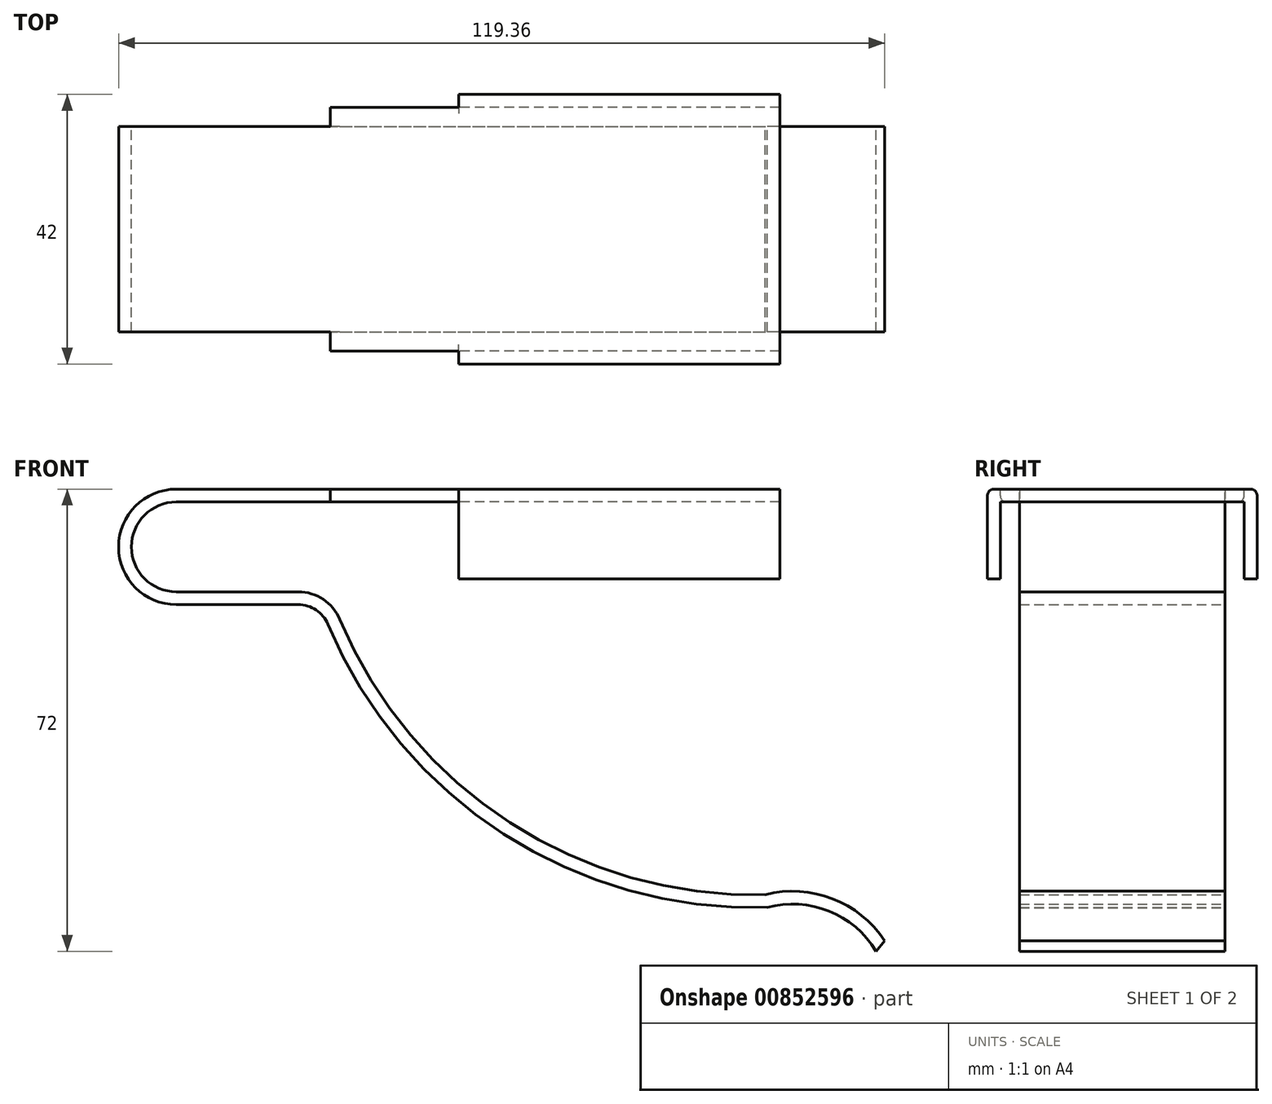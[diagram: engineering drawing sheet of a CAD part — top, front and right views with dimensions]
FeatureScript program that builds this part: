
annotation { "Feature Type Name" : "Feature", "Feature Type Description" : "" }
export const myFeature = defineFeature(function(context is Context, id is Id, definition is map)
    precondition{}
    {
        {
            var Q0;
            Q0=qCreatedBy(makeId("Front.planeOp"),FACE);
            var sketch = newSketch(context, id + "F0", { "sketchPlane" : qUnion([Q0])});
            skArc(sketch, "E0", {"start": v(0, 18) * mm, "mid": v(-9, 9) * mm, "end": v(0, 0) * mm});
            skLineSegment(sketch, "E1", {"start": v(0, 18) * mm, "end": v(94, 18) * mm});
            skLineSegment(sketch, "E2", {"start": v(0, 0) * mm, "end": v(19, 0) * mm});
            skArc(sketch, "E3", {"start": v(23.61, -3.06) * mm, "mid": v(50.99, -35.72) * mm, "end": v(92.03, -47.17) * mm});
            skArc(sketch, "E4", {"start": v(109.01, -54) * mm, "mid": v(101.66, -47.74) * mm, "end": v(92.03, -47.17) * mm});
            skPoint(sketch, "E5.visualSharp", {"position": v(22.4, 0) * mm});
            skArc(sketch, "E5.filletArc", {"start": v(23.61, -3.06) * mm, "mid": v(21.77, -0.84) * mm, "end": v(19, 0) * mm});
            skLineSegment(sketch, "E6.0", {"start": v(0, 16) * mm, "end": v(94, 16) * mm});
            skArc(sketch, "E6.1", {"start": v(0, 16) * mm, "mid": v(-7, 9) * mm, "end": v(0, 2) * mm});
            skArc(sketch, "E6.3", {"start": v(25.45, -2.3) * mm, "mid": v(51.98, -33.97) * mm, "end": v(91.74, -45.18) * mm});
            skArc(sketch, "E6.4", {"start": v(25.45, -2.3) * mm, "mid": v(22.88, 0.83) * mm, "end": v(19, 2) * mm});
            skLineSegment(sketch, "E6.5", {"start": v(0, 2) * mm, "end": v(19, 2) * mm});
            skLineSegment(sketch, "E7", {"start": v(94, 18) * mm, "end": v(94, 16) * mm});
            skLineSegment(sketch, "E8", {"start": v(110.36, -52.4) * mm, "end": v(109.01, -54) * mm});
            skPoint(sketch, "E9", {"position": v(0, 0) * mm});
            skArc(sketch, "E10.0", {"start": v(110.36, -52.4) * mm, "mid": v(102.2, -45.8) * mm, "end": v(91.74, -45.18) * mm});
            skSolve(sketch);
        }
        {
            var Q0;
            Q0=makeQuery(id+"F0.imprint","IMPRINT",FACE,{"disambiguationData":[TD([[makeQuery(id+"F0.imprint","IMPRINT",EDGE,{"derivedFrom":sQuery(id+"F0.wireOp",EDGE,"E0")}),1.0]])]});
            extrude(context, id + "F1", {"entities" : qUnion([Q0]), "depth" : 16 * mm, "offsetDistance" : 25 * mm});
        }
        {
            var Q0;
            Q0=makeQuery(id+"F1.opExtrude","SWEPT_FACE",FACE,{"disambiguationData":[OSD([sQuery(id+"F0.wireOp",EDGE,"E1")])]});
            var sketch = newSketch(context, id + "F2", { "sketchPlane" : qUnion([Q0])});
            skLineSegment(sketch, "E11.bottom", {"start": v(94, -16) * mm, "end": v(24, -16) * mm});
            skLineSegment(sketch, "E11.top", {"start": v(94, -19) * mm, "end": v(24, -19) * mm});
            skLineSegment(sketch, "E11.left", {"start": v(94, -16) * mm, "end": v(94, -19) * mm});
            skLineSegment(sketch, "E11.right", {"start": v(24, -16) * mm, "end": v(24, -19) * mm});
            skSolve(sketch);
        }
        {
            var Q0;
            Q0=makeQuery(id+"F2.imprint","IMPRINT",FACE,{"disambiguationData":[TD([[makeQuery(id+"F2.imprint","IMPRINT",EDGE,{"derivedFrom":sQuery(id+"F2.wireOp",EDGE,"E11.bottom")}),-1.0]])]});
            extrude(context, id + "F3", {"entities" : qUnion([Q0]), "operationType" : NewBodyOperationType.ADD, "oppositeDirection" : true, "depth" : 2 * mm, "offsetDistance" : 25 * mm});
        }
        {
            var Q0;
            Q0=makeQuery(id+"F3.opExtrude","SWEPT_FACE",FACE,{"disambiguationData":[OSD([sQuery(id+"F2.wireOp",EDGE,"E11.top")])]});
            var sketch = newSketch(context, id + "F4", { "sketchPlane" : qUnion([Q0])});
            skLineSegment(sketch, "E12.bottom", {"start": v(94, 18) * mm, "end": v(44, 18) * mm});
            skLineSegment(sketch, "E12.top", {"start": v(94, 4) * mm, "end": v(44, 4) * mm});
            skLineSegment(sketch, "E12.left", {"start": v(94, 18) * mm, "end": v(94, 4) * mm});
            skLineSegment(sketch, "E12.right", {"start": v(44, 18) * mm, "end": v(44, 4) * mm});
            skSolve(sketch);
        }
        {
            var Q0;
            Q0 = qSketchRegion(id + "F4", true);
            extrude(context, id + "F5", {"entities" : qUnion([Q0]), "operationType" : NewBodyOperationType.ADD, "depth" : 2 * mm, "offsetDistance" : 25 * mm});
        }
        {
            var Q0;
            Q0=makeQuery(id+"F5.opExtrude","CAP_EDGE",EDGE,{"disambiguationData":[OSD([sQuery(id+"F4.wireOp",EDGE,"E12.bottom")])],"isStart":false});
            var Q1;
            {var subQ0=sQuery(id+"F2.wireOp",EDGE,"E11.top");Q1=makeQuery(id+"F5.boolean.opBoolean","SPLIT",EDGE,{"disambiguationData":[topologyDisambiguationEdgeConnected([makeQuery(id+"F5.opExtrude","CAP_FACE",FACE,{"disambiguationData":[OSD([sQuery(id+"F4.wireOp",EDGE,"E12.bottom"),sQuery(id+"F4.wireOp",EDGE,"E12.top"),sQuery(id+"F4.wireOp",EDGE,"E12.left"),sQuery(id+"F4.wireOp",EDGE,"E12.right")])],"isStart":true})])],"derivedFrom":makeQuery(id+"F3.opExtrude","CAP_EDGE",EDGE,{"disambiguationData":[OSD([subQ0])],"isStart":false})});}
            fillet(context, id + "F6", {"entities" : qUnion([Q0, Q1]), "radius" : 1 * mm, "tangentPropagation" : true, "allowEdgeOverflow" : false});
        }
        {
            var Q0;
            Q0=makeQuery(id+"F1.opExtrude","SWEPT_BODY",BODY,{"disambiguationData":[OSD([sQuery(id+"F0.wireOp",EDGE,"E0"),sQuery(id+"F0.wireOp",EDGE,"E1"),sQuery(id+"F0.wireOp",EDGE,"E2"),sQuery(id+"F0.wireOp",EDGE,"E3"),sQuery(id+"F0.wireOp",EDGE,"E4"),sQuery(id+"F0.wireOp",EDGE,"E5.filletArc"),sQuery(id+"F0.wireOp",EDGE,"E6.0"),sQuery(id+"F0.wireOp",EDGE,"E6.1"),sQuery(id+"F0.wireOp",EDGE,"E6.3"),sQuery(id+"F0.wireOp",EDGE,"E6.4"),sQuery(id+"F0.wireOp",EDGE,"E6.5"),sQuery(id+"F0.wireOp",EDGE,"E7"),sQuery(id+"F0.wireOp",EDGE,"E8"),sQuery(id+"F0.wireOp",EDGE,"E10.0")])]});
            var Q1;
            Q1=qCreatedBy(makeId("Front.planeOp"),FACE);
            mirror(context, id + "F7", {"operationType" : NewBodyOperationType.ADD, "entities" : qUnion([Q0]), "mirrorPlane" : qUnion([Q1])});
        }
    });
